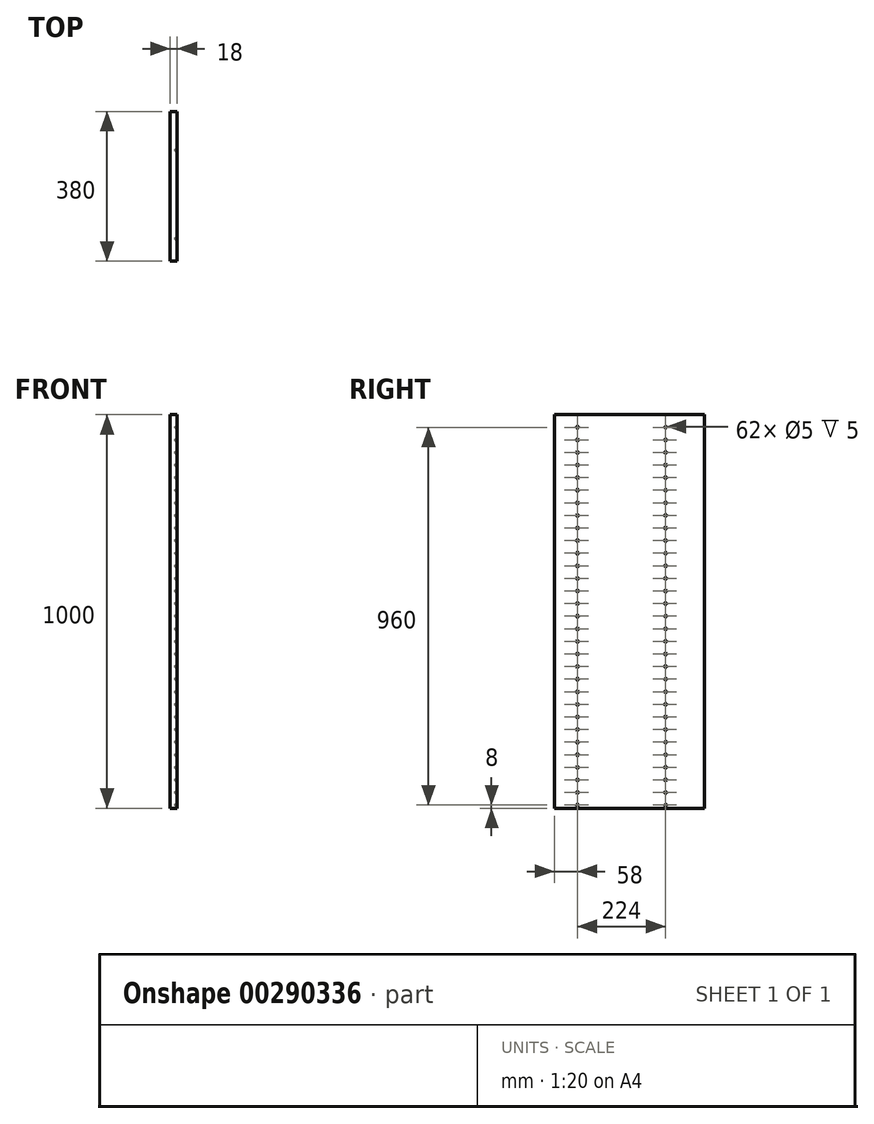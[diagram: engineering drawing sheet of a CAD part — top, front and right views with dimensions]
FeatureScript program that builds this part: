
annotation { "Feature Type Name" : "Feature", "Feature Type Description" : "" }
export const myFeature = defineFeature(function(context is Context, id is Id, definition is map)
    precondition{}
    {
        {
            var Q0;
            Q0=qCreatedBy(makeId("Right.planeOp"),FACE);
            var sketch = newSketch(context, id + "F0", { "sketchPlane" : qUnion([Q0])});
            skLineSegment(sketch, "E0.bottom", {"start": v(0, 0) * mm, "end": v(380, 0) * mm});
            skLineSegment(sketch, "E0.top", {"start": v(0, 1000) * mm, "end": v(380, 1000) * mm});
            skLineSegment(sketch, "E0.left", {"start": v(0, 0) * mm, "end": v(0, 1000) * mm});
            skLineSegment(sketch, "E0.right", {"start": v(380, 0) * mm, "end": v(380, 1000) * mm});
            skSolve(sketch);
        }
        {
            var Q0;
            Q0 = qSketchRegion(id + "F0", true);
            extrude(context, id + "F1", {"entities" : qUnion([Q0]), "depth" : 18 * mm});
        }
        {
            var Q0;
            Q0=makeQuery(id+"F1.opExtrude","CAP_FACE",FACE,{"disambiguationData":[OSD([sQuery(id+"F0.wireOp",EDGE,"E0.bottom"),sQuery(id+"F0.wireOp",EDGE,"E0.top"),sQuery(id+"F0.wireOp",EDGE,"E0.left"),sQuery(id+"F0.wireOp",EDGE,"E0.right")])],"isStart":false});
            var sketch = newSketch(context, id + "F2", { "sketchPlane" : qUnion([Q0])});
            skCircle(sketch, "E1", {"center": v(58, 8) * mm, "radius": 2.5 * mm});
            skCircle(sketch, "E2.0.1.0", {"center": v(58, 40) * mm, "radius": 2.5 * mm});
            skCircle(sketch, "E2.0.2.0", {"center": v(58, 72) * mm, "radius": 2.5 * mm});
            skCircle(sketch, "E2.0.3.0", {"center": v(58, 104) * mm, "radius": 2.5 * mm});
            skCircle(sketch, "E2.0.4.0", {"center": v(58, 136) * mm, "radius": 2.5 * mm});
            skCircle(sketch, "E2.0.5.0", {"center": v(58, 168) * mm, "radius": 2.5 * mm});
            skCircle(sketch, "E2.0.6.0", {"center": v(58, 200) * mm, "radius": 2.5 * mm});
            skCircle(sketch, "E2.0.7.0", {"center": v(58, 232) * mm, "radius": 2.5 * mm});
            skCircle(sketch, "E2.0.8.0", {"center": v(58, 264) * mm, "radius": 2.5 * mm});
            skCircle(sketch, "E2.0.9.0", {"center": v(58, 296) * mm, "radius": 2.5 * mm});
            skCircle(sketch, "E2.0.10.0", {"center": v(58, 328) * mm, "radius": 2.5 * mm});
            skCircle(sketch, "E2.0.11.0", {"center": v(58, 360) * mm, "radius": 2.5 * mm});
            skCircle(sketch, "E2.0.12.0", {"center": v(58, 392) * mm, "radius": 2.5 * mm});
            skCircle(sketch, "E2.0.13.0", {"center": v(58, 424) * mm, "radius": 2.5 * mm});
            skCircle(sketch, "E2.0.14.0", {"center": v(58, 456) * mm, "radius": 2.5 * mm});
            skCircle(sketch, "E2.0.15.0", {"center": v(58, 488) * mm, "radius": 2.5 * mm});
            skCircle(sketch, "E2.0.16.0", {"center": v(58, 520) * mm, "radius": 2.5 * mm});
            skCircle(sketch, "E2.0.17.0", {"center": v(58, 552) * mm, "radius": 2.5 * mm});
            skCircle(sketch, "E2.0.18.0", {"center": v(58, 584) * mm, "radius": 2.5 * mm});
            skCircle(sketch, "E2.0.19.0", {"center": v(58, 616) * mm, "radius": 2.5 * mm});
            skCircle(sketch, "E2.0.20.0", {"center": v(58, 648) * mm, "radius": 2.5 * mm});
            skCircle(sketch, "E2.0.21.0", {"center": v(58, 680) * mm, "radius": 2.5 * mm});
            skCircle(sketch, "E2.0.22.0", {"center": v(58, 712) * mm, "radius": 2.5 * mm});
            skCircle(sketch, "E2.0.23.0", {"center": v(58, 744) * mm, "radius": 2.5 * mm});
            skCircle(sketch, "E2.0.24.0", {"center": v(58, 776) * mm, "radius": 2.5 * mm});
            skCircle(sketch, "E2.0.25.0", {"center": v(58, 808) * mm, "radius": 2.5 * mm});
            skCircle(sketch, "E2.0.26.0", {"center": v(58, 840) * mm, "radius": 2.5 * mm});
            skCircle(sketch, "E2.0.27.0", {"center": v(58, 872) * mm, "radius": 2.5 * mm});
            skCircle(sketch, "E2.0.28.0", {"center": v(58, 904) * mm, "radius": 2.5 * mm});
            skCircle(sketch, "E2.0.29.0", {"center": v(58, 936) * mm, "radius": 2.5 * mm});
            skCircle(sketch, "E2.0.30.0", {"center": v(58, 968) * mm, "radius": 2.5 * mm});
            skLineSegment(sketch, "E2.direction1", {"start": v(58, 8) * mm, "end": v(83, 8) * mm, "construction": true});
            skLineSegment(sketch, "E2.direction2", {"start": v(58, 8) * mm, "end": v(58, 40) * mm, "construction": true});
            skCircle(sketch, "E3", {"center": v(282, 8) * mm, "radius": 2.5 * mm});
            skCircle(sketch, "E4.0.1.0", {"center": v(282, 40) * mm, "radius": 2.5 * mm});
            skCircle(sketch, "E4.0.2.0", {"center": v(282, 72) * mm, "radius": 2.5 * mm});
            skCircle(sketch, "E4.0.3.0", {"center": v(282, 104) * mm, "radius": 2.5 * mm});
            skCircle(sketch, "E4.0.4.0", {"center": v(282, 136) * mm, "radius": 2.5 * mm});
            skCircle(sketch, "E4.0.5.0", {"center": v(282, 168) * mm, "radius": 2.5 * mm});
            skCircle(sketch, "E4.0.6.0", {"center": v(282, 200) * mm, "radius": 2.5 * mm});
            skCircle(sketch, "E4.0.7.0", {"center": v(282, 232) * mm, "radius": 2.5 * mm});
            skCircle(sketch, "E4.0.8.0", {"center": v(282, 264) * mm, "radius": 2.5 * mm});
            skCircle(sketch, "E4.0.9.0", {"center": v(282, 296) * mm, "radius": 2.5 * mm});
            skCircle(sketch, "E4.0.10.0", {"center": v(282, 328) * mm, "radius": 2.5 * mm});
            skCircle(sketch, "E4.0.11.0", {"center": v(282, 360) * mm, "radius": 2.5 * mm});
            skCircle(sketch, "E4.0.12.0", {"center": v(282, 392) * mm, "radius": 2.5 * mm});
            skCircle(sketch, "E4.0.13.0", {"center": v(282, 424) * mm, "radius": 2.5 * mm});
            skCircle(sketch, "E4.0.14.0", {"center": v(282, 456) * mm, "radius": 2.5 * mm});
            skCircle(sketch, "E4.0.15.0", {"center": v(282, 488) * mm, "radius": 2.5 * mm});
            skCircle(sketch, "E4.0.16.0", {"center": v(282, 520) * mm, "radius": 2.5 * mm});
            skCircle(sketch, "E4.0.17.0", {"center": v(282, 552) * mm, "radius": 2.5 * mm});
            skCircle(sketch, "E4.0.18.0", {"center": v(282, 584) * mm, "radius": 2.5 * mm});
            skCircle(sketch, "E4.0.19.0", {"center": v(282, 616) * mm, "radius": 2.5 * mm});
            skCircle(sketch, "E4.0.20.0", {"center": v(282, 648) * mm, "radius": 2.5 * mm});
            skCircle(sketch, "E4.0.21.0", {"center": v(282, 680) * mm, "radius": 2.5 * mm});
            skCircle(sketch, "E4.0.22.0", {"center": v(282, 712) * mm, "radius": 2.5 * mm});
            skCircle(sketch, "E4.0.23.0", {"center": v(282, 744) * mm, "radius": 2.5 * mm});
            skCircle(sketch, "E4.0.24.0", {"center": v(282, 776) * mm, "radius": 2.5 * mm});
            skCircle(sketch, "E4.0.25.0", {"center": v(282, 808) * mm, "radius": 2.5 * mm});
            skCircle(sketch, "E4.0.26.0", {"center": v(282, 840) * mm, "radius": 2.5 * mm});
            skCircle(sketch, "E4.0.27.0", {"center": v(282, 872) * mm, "radius": 2.5 * mm});
            skCircle(sketch, "E4.0.28.0", {"center": v(282, 904) * mm, "radius": 2.5 * mm});
            skCircle(sketch, "E4.0.29.0", {"center": v(282, 936) * mm, "radius": 2.5 * mm});
            skCircle(sketch, "E4.0.30.0", {"center": v(282, 968) * mm, "radius": 2.5 * mm});
            skLineSegment(sketch, "E4.direction1", {"start": v(282, 8) * mm, "end": v(850.92, 8) * mm, "construction": true});
            skLineSegment(sketch, "E4.direction2", {"start": v(282, 8) * mm, "end": v(282, 40) * mm, "construction": true});
            skSolve(sketch);
        }
        {
            var Q0;
            Q0 = qSketchRegion(id + "F2", true);
            extrude(context, id + "F3", {"entities" : qUnion([Q0]), "operationType" : NewBodyOperationType.REMOVE, "oppositeDirection" : true, "depth" : 5 * mm});
        }
    });
